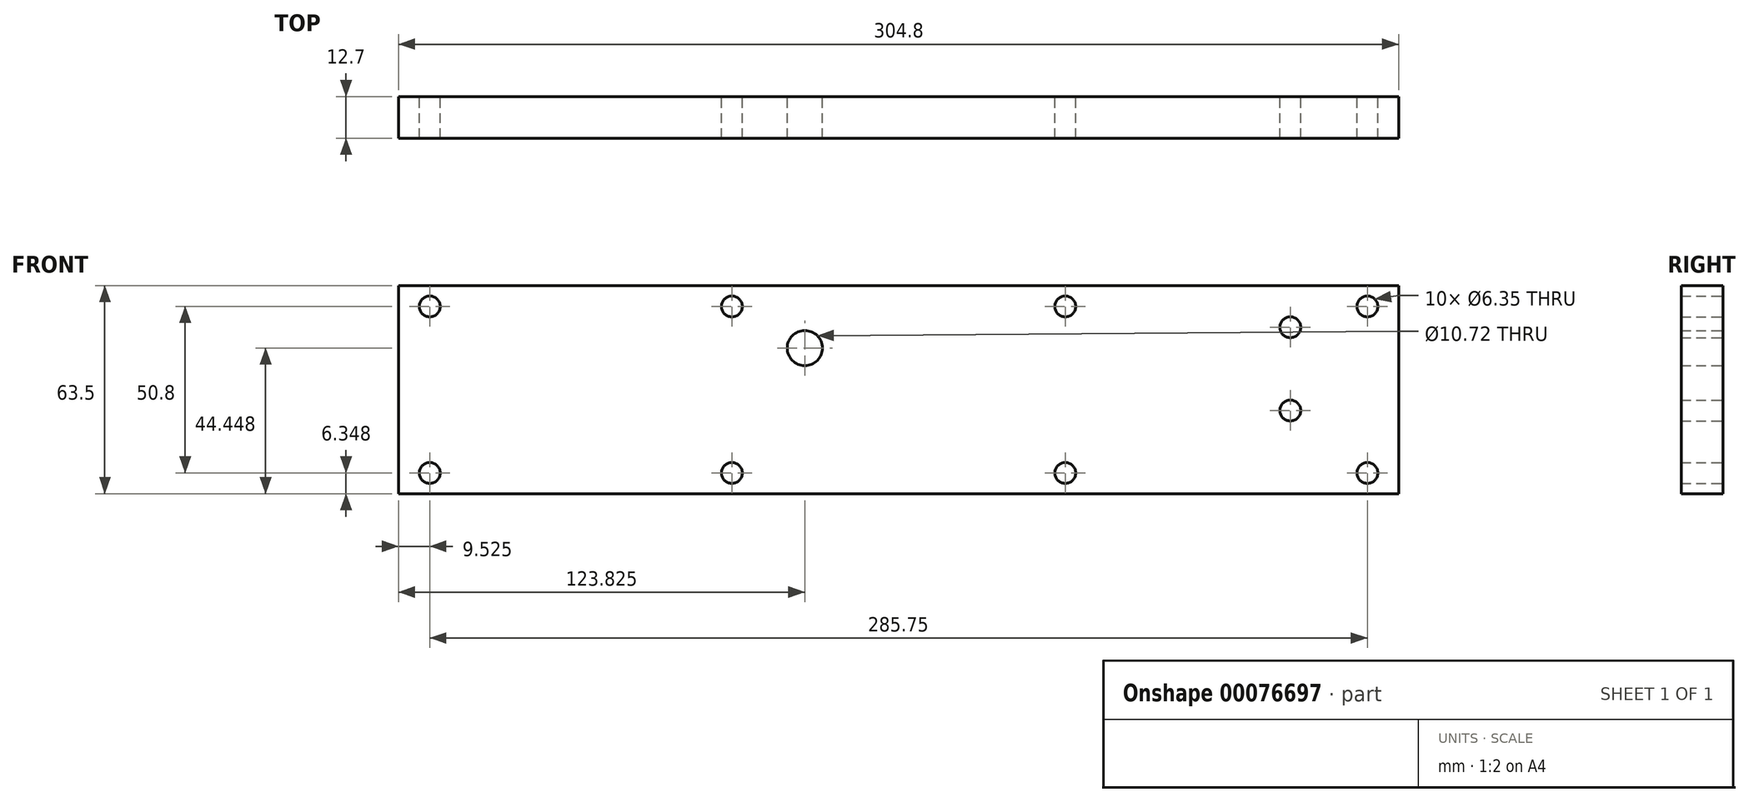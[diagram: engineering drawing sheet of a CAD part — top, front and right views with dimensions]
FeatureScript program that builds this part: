
annotation { "Feature Type Name" : "Feature", "Feature Type Description" : "" }
export const myFeature = defineFeature(function(context is Context, id is Id, definition is map)
    precondition{}
    {
        {
            var Q0;
            Q0=qCreatedBy(makeId("Front.planeOp"),FACE);
            var sketch = newSketch(context, id + "F0", { "sketchPlane" : qUnion([Q0])});
            skLineSegment(sketch, "E0.bottom", {"start": v(-155.17, 43.3) * mm, "end": v(149.63, 43.3) * mm});
            skLineSegment(sketch, "E0.top", {"start": v(-155.17, -20.2) * mm, "end": v(149.63, -20.2) * mm});
            skLineSegment(sketch, "E0.left", {"start": v(-155.17, 43.3) * mm, "end": v(-155.17, -20.2) * mm});
            skLineSegment(sketch, "E0.right", {"start": v(149.63, 43.3) * mm, "end": v(149.63, -20.2) * mm});
            skCircle(sketch, "E1", {"center": v(-145.64, 36.95) * mm, "radius": 3.18 * mm});
            skCircle(sketch, "E2", {"center": v(-53.57, 36.95) * mm, "radius": 3.18 * mm});
            skCircle(sketch, "E3", {"center": v(48.03, 36.95) * mm, "radius": 3.18 * mm});
            skCircle(sketch, "E4", {"center": v(140.1, 36.95) * mm, "radius": 3.18 * mm});
            skCircle(sketch, "E5", {"center": v(140.1, -13.85) * mm, "radius": 3.18 * mm});
            skCircle(sketch, "E6", {"center": v(48.03, -13.85) * mm, "radius": 3.18 * mm});
            skCircle(sketch, "E7", {"center": v(-53.57, -13.85) * mm, "radius": 3.18 * mm});
            skCircle(sketch, "E8", {"center": v(-145.64, -13.85) * mm, "radius": 3.18 * mm});
            skLineSegment(sketch, "E9.0", {"start": v(-155.17, 30.6) * mm, "end": v(149.63, 30.6) * mm, "construction": true});
            skLineSegment(sketch, "E10.0", {"start": v(116.61, 43.3) * mm, "end": v(116.61, -20.2) * mm, "construction": true});
            skLineSegment(sketch, "E11.0", {"start": v(-155.17, 5.2) * mm, "end": v(149.63, 5.2) * mm, "construction": true});
            skCircle(sketch, "E12", {"center": v(116.61, 30.6) * mm, "radius": 3.18 * mm});
            skCircle(sketch, "E13", {"center": v(116.61, 5.2) * mm, "radius": 3.18 * mm});
            skCircle(sketch, "E14", {"center": v(-31.34, 24.25) * mm, "radius": 5.36 * mm});
            skSolve(sketch);
        }
        {
            var Q0;
            Q0=makeQuery(id+"F0.imprint","IMPRINT",FACE,{"disambiguationData":[TD([[makeQuery(id+"F0.imprint","IMPRINT",EDGE,{"derivedFrom":sQuery(id+"F0.wireOp",EDGE,"E0.bottom")}),-1.0]])]});
            extrude(context, id + "F1", {"entities" : qUnion([Q0]), "depth" : 12.7 * mm});
        }
    });
